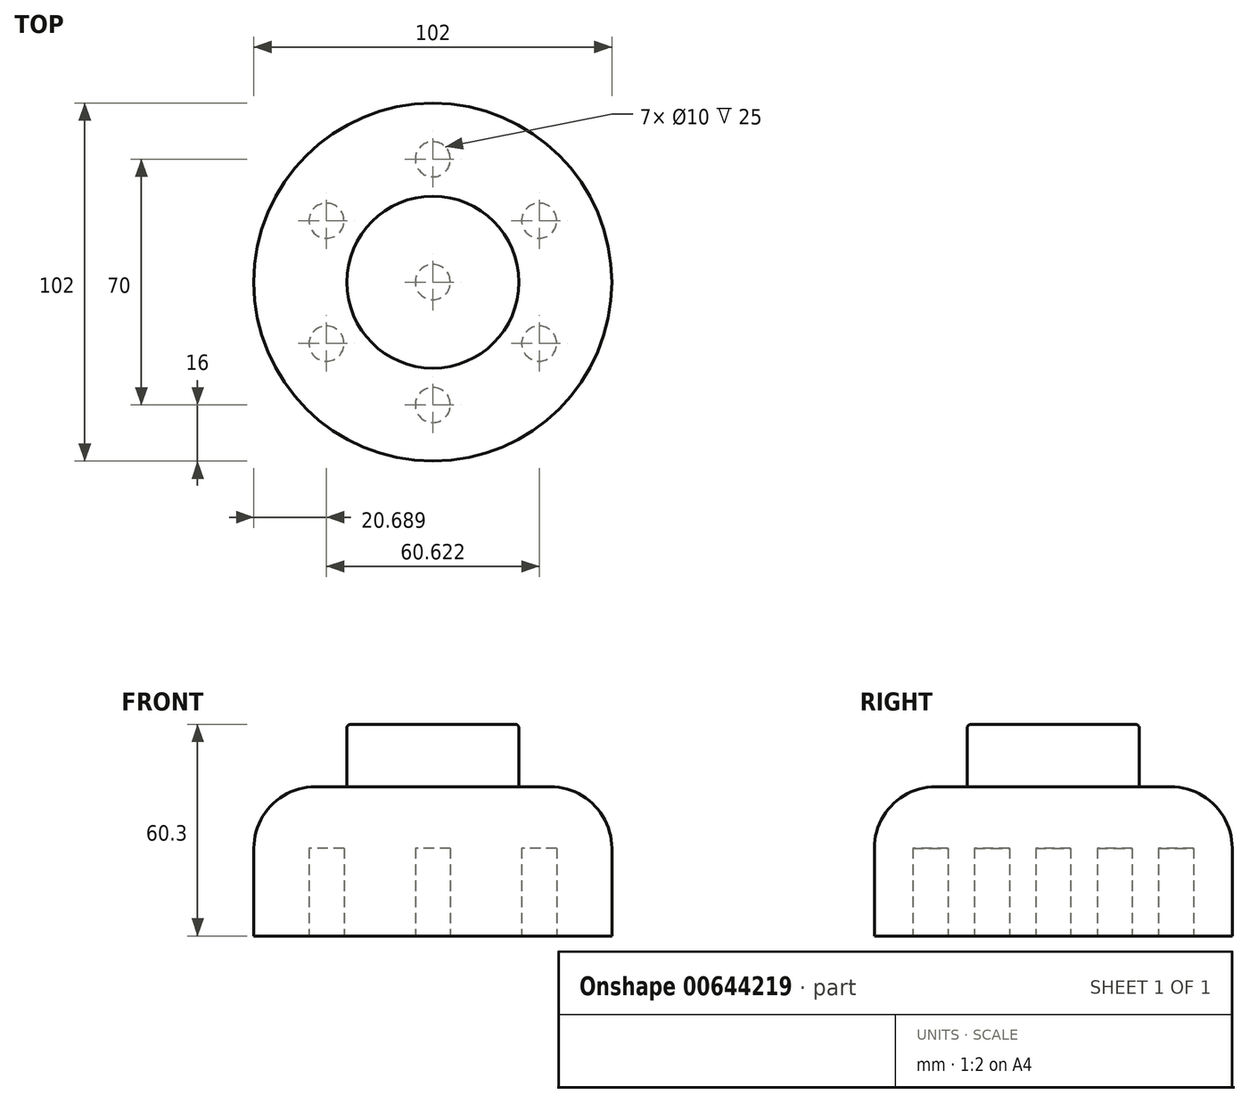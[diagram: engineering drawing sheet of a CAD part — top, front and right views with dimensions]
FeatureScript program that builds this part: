
annotation { "Feature Type Name" : "Feature", "Feature Type Description" : "" }
export const myFeature = defineFeature(function(context is Context, id is Id, definition is map)
    precondition{}
    {
        {
            var Q0;
            Q0=qCreatedBy(makeId("Top.planeOp"),FACE);
            var sketch = newSketch(context, id + "F0", { "sketchPlane" : qUnion([Q0])});
            skCircle(sketch, "E0", {"center": v(0, 0) * mm, "radius": 51 * mm});
            skSolve(sketch);
        }
        {
            var Q0;
            Q0=makeQuery(id+"F0.imprint","IMPRINT",FACE,{"disambiguationData":[TD([[makeQuery(id+"F0.imprint","IMPRINT",EDGE,{"derivedFrom":sQuery(id+"F0.wireOp",EDGE,"E0")}),1.0]])]});
            extrude(context, id + "F1", {"entities" : qUnion([Q0]), "depth" : 42.5 * mm});
        }
        {
            var Q0;
            Q0=qCreatedBy(makeId("Top.planeOp"),FACE);
            var sketch = newSketch(context, id + "F2", { "sketchPlane" : qUnion([Q0])});
            skCircle(sketch, "E1", {"center": v(0, 0) * mm, "radius": 5 * mm});
            skCircle(sketch, "E2", {"center": v(0, -35) * mm, "radius": 5 * mm});
            skCircle(sketch, "E3.1.0", {"center": v(30.31, -17.5) * mm, "radius": 5 * mm});
            skCircle(sketch, "E3.2.0", {"center": v(30.31, 17.5) * mm, "radius": 5 * mm});
            skCircle(sketch, "E3.3.0", {"center": v(0, 35) * mm, "radius": 5 * mm});
            skCircle(sketch, "E3.4.0", {"center": v(-30.31, 17.5) * mm, "radius": 5 * mm});
            skCircle(sketch, "E3.5.0", {"center": v(-30.31, -17.5) * mm, "radius": 5 * mm});
            skSolve(sketch);
        }
        {
            var Q0;
            Q0=makeQuery(id+"F2.imprint","IMPRINT",FACE,{"disambiguationData":[TD([[makeQuery(id+"F2.imprint","IMPRINT",EDGE,{"derivedFrom":sQuery(id+"F2.wireOp",EDGE,"E2")}),1.0]])]});
            var Q1;
            Q1=makeQuery(id+"F2.imprint","IMPRINT",FACE,{"disambiguationData":[TD([[makeQuery(id+"F2.imprint","IMPRINT",EDGE,{"derivedFrom":sQuery(id+"F2.wireOp",EDGE,"E3.1.0")}),1.0]])]});
            var Q2;
            Q2=makeQuery(id+"F2.imprint","IMPRINT",FACE,{"disambiguationData":[TD([[makeQuery(id+"F2.imprint","IMPRINT",EDGE,{"derivedFrom":sQuery(id+"F2.wireOp",EDGE,"E3.2.0")}),1.0]])]});
            var Q3;
            Q3=makeQuery(id+"F2.imprint","IMPRINT",FACE,{"disambiguationData":[TD([[makeQuery(id+"F2.imprint","IMPRINT",EDGE,{"derivedFrom":sQuery(id+"F2.wireOp",EDGE,"E3.3.0")}),1.0]])]});
            var Q4;
            Q4=makeQuery(id+"F2.imprint","IMPRINT",FACE,{"disambiguationData":[TD([[makeQuery(id+"F2.imprint","IMPRINT",EDGE,{"derivedFrom":sQuery(id+"F2.wireOp",EDGE,"E3.4.0")}),1.0]])]});
            var Q5;
            Q5=makeQuery(id+"F2.imprint","IMPRINT",FACE,{"disambiguationData":[TD([[makeQuery(id+"F2.imprint","IMPRINT",EDGE,{"derivedFrom":sQuery(id+"F2.wireOp",EDGE,"E3.5.0")}),1.0]])]});
            var Q6;
            Q6=makeQuery(id+"F2.imprint","IMPRINT",FACE,{"disambiguationData":[TD([[makeQuery(id+"F2.imprint","IMPRINT",EDGE,{"derivedFrom":sQuery(id+"F2.wireOp",EDGE,"E1")}),1.0]])]});
            extrude(context, id + "F3", {"entities" : qUnion([Q0, Q1, Q2, Q3, Q4, Q5, Q6]), "operationType" : NewBodyOperationType.REMOVE, "oppositeDirection" : true, "depth" : -25 * mm});
        }
        {
            var Q0;
            Q0=makeQuery(id+"F1.opExtrude","CAP_EDGE",EDGE,{"disambiguationData":[OSD([sQuery(id+"F0.wireOp",EDGE,"E0")])],"isStart":false});
            fillet(context, id + "F4", {"entities" : qUnion([Q0]), "radius" : 17.5 * mm, "tangentPropagation" : true, "allowEdgeOverflow" : false});
        }
        {
            var Q0;
            Q0=makeQuery(id+"F1.opExtrude","CAP_FACE",FACE,{"disambiguationData":[OSD([sQuery(id+"F0.wireOp",EDGE,"E0")])],"isStart":false});
            var sketch = newSketch(context, id + "F5", { "sketchPlane" : qUnion([Q0])});
            skCircle(sketch, "E4", {"center": v(0, 0) * mm, "radius": 24.5 * mm});
            skSolve(sketch);
        }
        {
            var Q0;
            Q0=makeQuery(id+"F5.imprint","IMPRINT",FACE,{"disambiguationData":[TD([[makeQuery(id+"F5.imprint","IMPRINT",EDGE,{"derivedFrom":sQuery(id+"F5.wireOp",EDGE,"E4")}),1.0]])]});
            extrude(context, id + "F6", {"entities" : qUnion([Q0]), "operationType" : NewBodyOperationType.ADD, "depth" : 17.8 * mm});
        }
        {
            var Q0;
            Q0=makeQuery(id+"F6.opExtrude","CAP_EDGE",EDGE,{"disambiguationData":[OSD([sQuery(id+"F5.wireOp",EDGE,"E4")])],"isStart":false});
            fillet(context, id + "F7", {"entities" : qUnion([Q0]), "radius" : 1 * mm, "tangentPropagation" : true, "allowEdgeOverflow" : false});
        }
    });
